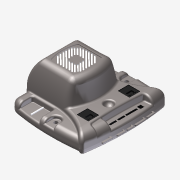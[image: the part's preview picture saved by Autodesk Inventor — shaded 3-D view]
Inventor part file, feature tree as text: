
AUTODESK INVENTOR PART (.ipt)
format: ipt  version: 2013 (Build 170138000, 138)  size: 5,713,408 bytes
history: native  units: mm
features: extrude x8, sketch x6, mirror x3, plane x2, other x2, imported_body x1
ambient origin geometry x8: Origin, YZ Plane, XZ Plane, XY Plane, X Axis, Y Axis, Z Axis, Center Point
bodies: Solid1 (feature_tree)
feature tree (22):
  imported_body  "Base1"
  sketch  "Sketch1"  dims[d50=0.9144mm d57=1.467403mm]
  extrude  "Extrusion2"  Depth=1.467403mm
  plane  "Work Plane1"
  mirror  "Mirror1"
  extrude  "Extrusion3"  Depth=1.467403mm
  sketch  "Sketch2"  dims[d58=1.467403mm d59=1.467403mm]
  extrude  "Extrusion4"  Depth=1.467403mm
  extrude  "Extrusion6"  Depth=1.467403mm
  extrude  "Extrusion7"  TaperAngle=90.0deg  [1 undecoded]
  mirror  "Mirror2"
  extrude  "Extrusion8"  Depth=9.7282mm
  mirror  "Mirror3"
  sketch  "Sketch5"  dims[d62=1.467403mm d63=1.467403mm]
  other  "Work Axis1"
  extrude  "Extrusion9"  Depth=0.762mm TaperAngle=0.0deg
  plane  "Work Plane2"
  extrude  "Extrusion10"  Depth=0.762mm
  sketch  "Sketch4"  dims[d60=1.467403mm d61=1.467403mm]
  sketch  "Sketch6"  dims[d66=1.27mm d67=0.0mm d70=90.0deg]
  sketch  "Sketch7"  dims[d71=1.27mm d72=0.0mm d73=9.7282mm d75=0.762mm d76=0.0mm d77=0.762mm d80=2.54mm d81=0.0mm d82=0.254mm d83=0.0mm d84=1.016mm d85=0.0mm d86=1.27mm d87=2.286mm d88=4.572mm d89=4.572mm d90=3.81mm d91=0.0mm d92=-15.24mm d105=129.575698mm d160=0.254mm d162=1.27mm d169=0.635mm d182=1.27mm d183=0.0mm]
  other  "Image2"
note: 1 required parameter value undecoded (feature->parameter linkage not recoverable at this tier; creation-order binding heuristic only, values carry confidence <= 0.55)
